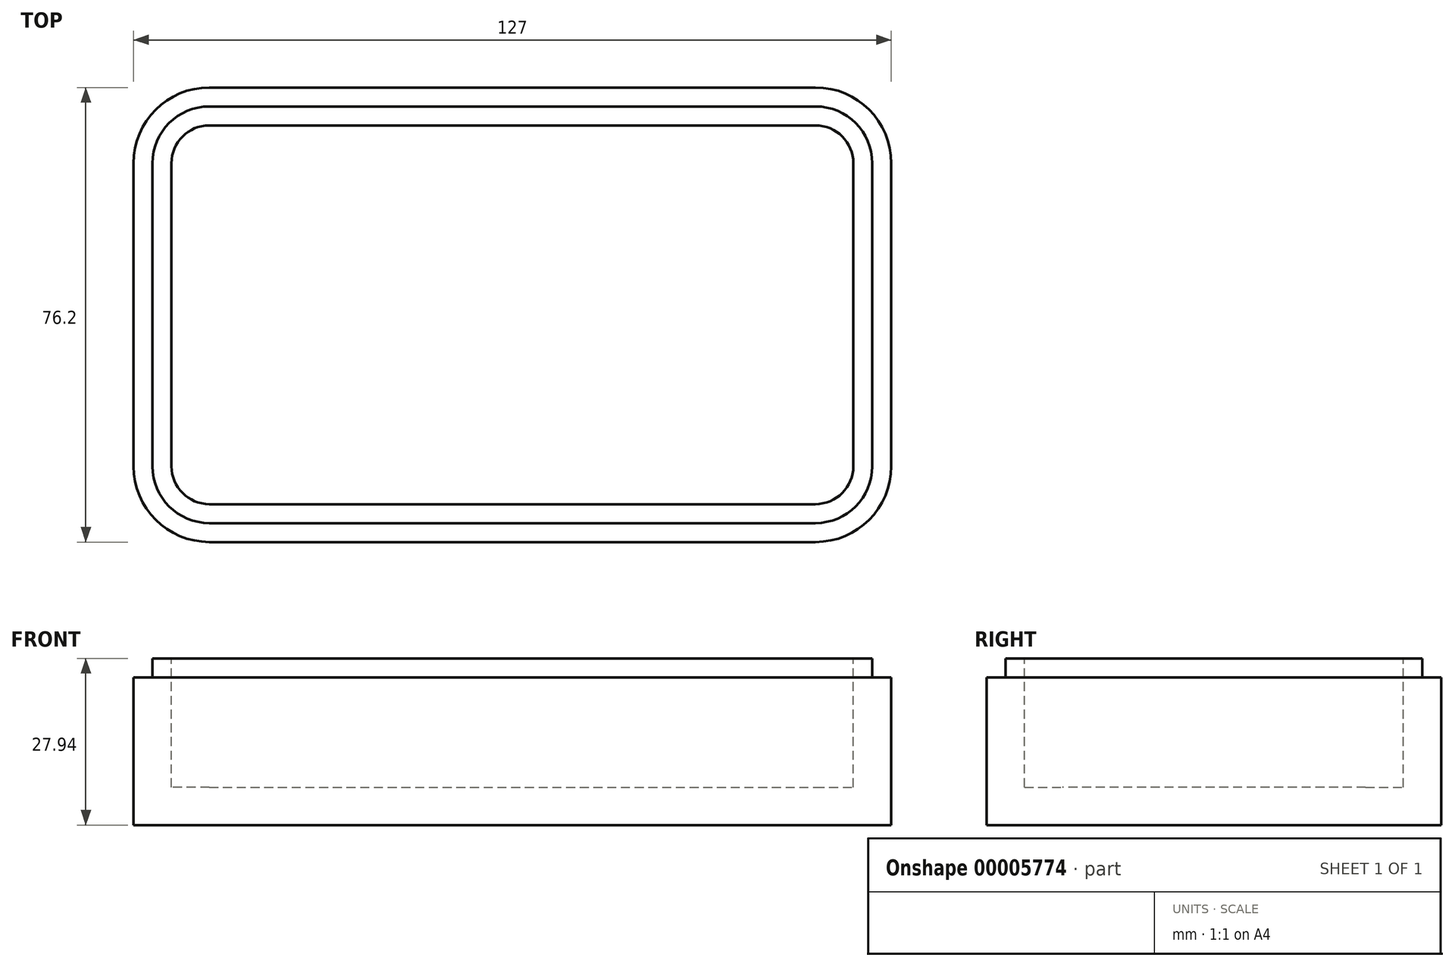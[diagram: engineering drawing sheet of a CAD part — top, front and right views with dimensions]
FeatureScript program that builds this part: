
annotation { "Feature Type Name" : "Feature", "Feature Type Description" : "" }
export const myFeature = defineFeature(function(context is Context, id is Id, definition is map)
    precondition{}
    {
        {
            var Q0;
            Q0=qCreatedBy(makeId("Top.planeOp"),FACE);
            var sketch = newSketch(context, id + "F0", { "sketchPlane" : qUnion([Q0])});
            skLineSegment(sketch, "E0.bottom", {"start": v(12.7, 0) * mm, "end": v(114.3, 0) * mm});
            skLineSegment(sketch, "E0.top", {"start": v(12.7, 76.2) * mm, "end": v(114.3, 76.2) * mm});
            skLineSegment(sketch, "E0.left", {"start": v(0, 12.7) * mm, "end": v(0, 63.5) * mm});
            skLineSegment(sketch, "E0.right", {"start": v(127, 12.7) * mm, "end": v(127, 63.5) * mm});
            skPoint(sketch, "E1.visualSharp", {"position": v(0, 0) * mm});
            skArc(sketch, "E1.filletArc", {"start": v(0, 12.7) * mm, "mid": v(3.72, 3.72) * mm, "end": v(12.7, 0) * mm});
            skPoint(sketch, "E2.visualSharp", {"position": v(0, 76.2) * mm});
            skArc(sketch, "E2.filletArc", {"start": v(12.7, 76.2) * mm, "mid": v(3.72, 72.48) * mm, "end": v(0, 63.5) * mm});
            skPoint(sketch, "E3.visualSharp", {"position": v(127, 76.2) * mm});
            skArc(sketch, "E3.filletArc", {"start": v(127, 63.5) * mm, "mid": v(123.28, 72.48) * mm, "end": v(114.3, 76.2) * mm});
            skPoint(sketch, "E4.visualSharp", {"position": v(127, 0) * mm});
            skArc(sketch, "E4.filletArc", {"start": v(114.3, 0) * mm, "mid": v(123.28, 3.72) * mm, "end": v(127, 12.7) * mm});
            skLineSegment(sketch, "E5.0", {"start": v(12.7, 73.03) * mm, "end": v(114.3, 73.03) * mm});
            skArc(sketch, "E5.1", {"start": v(123.82, 63.5) * mm, "mid": v(121.04, 70.24) * mm, "end": v(114.3, 73.02) * mm});
            skLineSegment(sketch, "E5.2", {"start": v(123.83, 12.7) * mm, "end": v(123.82, 63.5) * mm});
            skArc(sketch, "E5.3", {"start": v(114.3, 3.18) * mm, "mid": v(121.04, 5.96) * mm, "end": v(123.83, 12.7) * mm});
            skLineSegment(sketch, "E5.4", {"start": v(12.7, 3.18) * mm, "end": v(114.3, 3.18) * mm});
            skArc(sketch, "E5.5", {"start": v(12.7, 73.03) * mm, "mid": v(5.96, 70.24) * mm, "end": v(3.17, 63.5) * mm});
            skArc(sketch, "E5.6", {"start": v(3.17, 12.7) * mm, "mid": v(5.96, 5.96) * mm, "end": v(12.7, 3.18) * mm});
            skLineSegment(sketch, "E5.7", {"start": v(3.17, 12.7) * mm, "end": v(3.17, 63.5) * mm});
            skArc(sketch, "E6.0", {"start": v(12.7, 69.85) * mm, "mid": v(8.2, 68) * mm, "end": v(6.35, 63.5) * mm});
            skLineSegment(sketch, "E6.1", {"start": v(6.35, 12.7) * mm, "end": v(6.35, 63.5) * mm});
            skArc(sketch, "E6.2", {"start": v(6.35, 12.7) * mm, "mid": v(8.2, 8.2) * mm, "end": v(12.7, 6.35) * mm});
            skLineSegment(sketch, "E6.3", {"start": v(12.7, 6.35) * mm, "end": v(114.3, 6.35) * mm});
            skArc(sketch, "E6.4", {"start": v(114.3, 6.35) * mm, "mid": v(118.8, 8.2) * mm, "end": v(120.65, 12.7) * mm});
            skLineSegment(sketch, "E6.5", {"start": v(12.7, 69.85) * mm, "end": v(114.3, 69.85) * mm});
            skLineSegment(sketch, "E6.6", {"start": v(120.65, 12.7) * mm, "end": v(120.65, 63.5) * mm});
            skArc(sketch, "E6.7", {"start": v(120.65, 63.5) * mm, "mid": v(118.8, 68) * mm, "end": v(114.3, 69.85) * mm});
            skSolve(sketch);
        }
        {
            var Q0;
            Q0=makeQuery(id+"F0.imprint","IMPRINT",FACE,{"disambiguationData":[TD([[makeQuery(id+"F0.imprint","IMPRINT",EDGE,{"derivedFrom":sQuery(id+"F0.wireOp",EDGE,"E5.0")}),-1.0]])]});
            var Q1;
            Q1=makeQuery(id+"F0.imprint","IMPRINT",FACE,{"disambiguationData":[TD([[makeQuery(id+"F0.imprint","IMPRINT",EDGE,{"derivedFrom":sQuery(id+"F0.wireOp",EDGE,"E6.0")}),1.0]])]});
            var Q2;
            Q2=makeQuery(id+"F0.imprint","IMPRINT",FACE,{"disambiguationData":[TD([[makeQuery(id+"F0.imprint","IMPRINT",EDGE,{"derivedFrom":sQuery(id+"F0.wireOp",EDGE,"E0.bottom")}),1.0]])]});
            extrude(context, id + "F1", {"entities" : qUnion([Q0, Q1, Q2]), "depth" : 27.94 * mm});
        }
        {
            var Q0;
            Q0=makeQuery(id+"F0.imprint","IMPRINT",FACE,{"disambiguationData":[TD([[makeQuery(id+"F0.imprint","IMPRINT",EDGE,{"derivedFrom":sQuery(id+"F0.wireOp",EDGE,"E0.bottom")}),1.0]])]});
            extrude(context, id + "F2", {"entities" : qUnion([Q0]), "operationType" : NewBodyOperationType.REMOVE, "depth" : 3.17 * mm});
        }
        {
            var Q0;
            Q0=makeQuery(id+"F0.imprint","IMPRINT",FACE,{"disambiguationData":[TD([[makeQuery(id+"F0.imprint","IMPRINT",EDGE,{"derivedFrom":sQuery(id+"F0.wireOp",EDGE,"E6.0")}),1.0]])]});
            extrude(context, id + "F3", {"entities" : qUnion([Q0]), "operationType" : NewBodyOperationType.REMOVE, "depth" : 21.59 * mm});
        }
        {
            var Q0;
            Q0=makeQuery(id+"F1.opExtrude","SWEPT_BODY",BODY,{"disambiguationData":[OSD([sQuery(id+"F0.wireOp",EDGE,"E0.bottom"),sQuery(id+"F0.wireOp",EDGE,"E0.top"),sQuery(id+"F0.wireOp",EDGE,"E0.left"),sQuery(id+"F0.wireOp",EDGE,"E0.right"),sQuery(id+"F0.wireOp",EDGE,"E1.filletArc"),sQuery(id+"F0.wireOp",EDGE,"E2.filletArc"),sQuery(id+"F0.wireOp",EDGE,"E3.filletArc"),sQuery(id+"F0.wireOp",EDGE,"E4.filletArc")])]});
            var Q1;
            Q1=sQuery(id+"F0.wireOp",EDGE,"E0.bottom");
            transform(context, id + "F4", {"entities" : qUnion([Q0]), "transformType" : TransformType.ROTATION, "transformAxis" : qUnion([Q1]), "angle" : 180 * degree, "makeCopy" : false});
        }
    });
